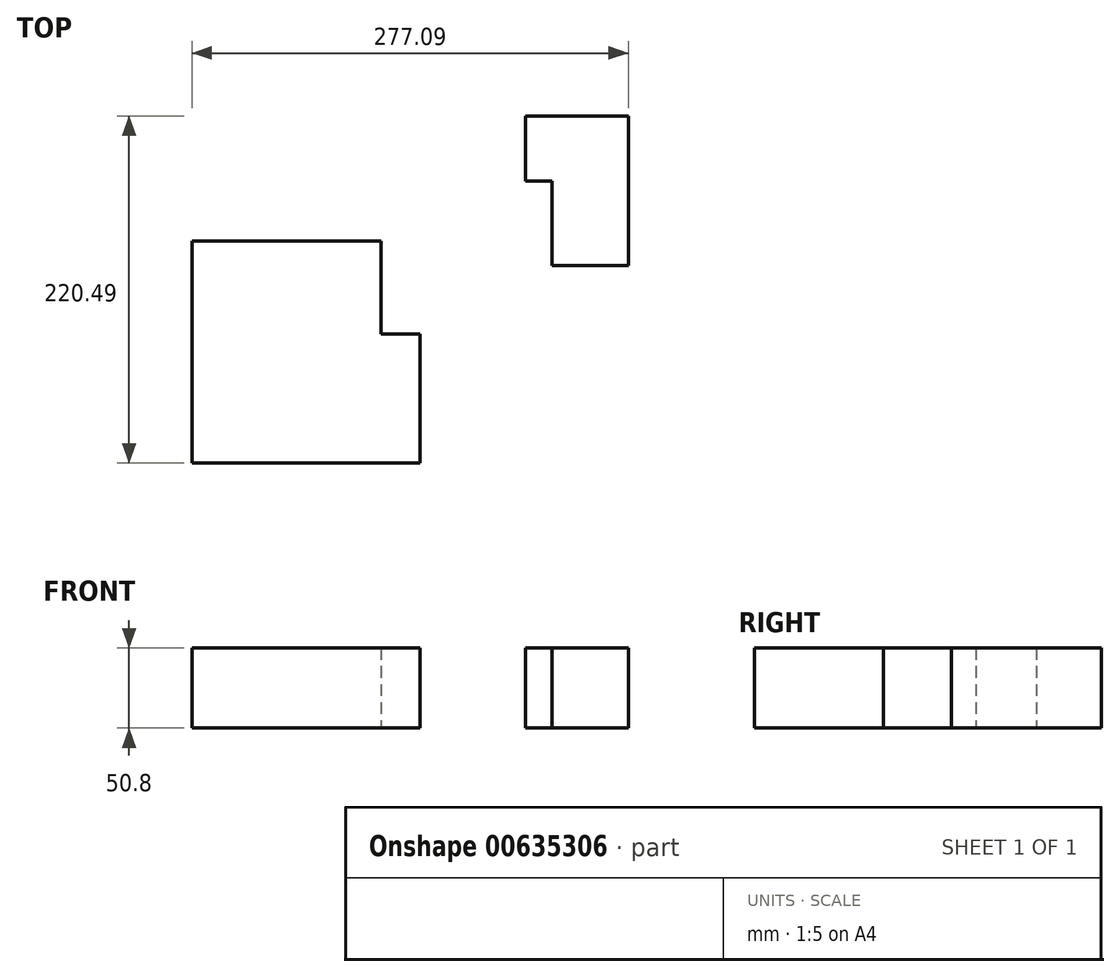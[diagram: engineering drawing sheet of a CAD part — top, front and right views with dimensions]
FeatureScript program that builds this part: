
annotation { "Feature Type Name" : "Feature", "Feature Type Description" : "" }
export const myFeature = defineFeature(function(context is Context, id is Id, definition is map)
    precondition{}
    {
        {
            var Q0;
            Q0=qCreatedBy(makeId("Top.planeOp"),FACE);
            var sketch = newSketch(context, id + "F0", { "sketchPlane" : qUnion([Q0])});
            skLineSegment(sketch, "E0.bottom", {"start": v(-75.4, 140.88) * mm, "end": v(69.35, 140.88) * mm});
            skLineSegment(sketch, "E0.top", {"start": v(-75.4, 0) * mm, "end": v(69.35, 0) * mm});
            skLineSegment(sketch, "E0.left", {"start": v(-75.4, 140.88) * mm, "end": v(-75.4, 0) * mm});
            skLineSegment(sketch, "E0.right", {"start": v(69.35, 140.88) * mm, "end": v(69.35, 0) * mm});
            skLineSegment(sketch, "E1.bottom", {"start": v(44.54, 179.13) * mm, "end": v(153.1, 179.13) * mm});
            skLineSegment(sketch, "E1.top", {"start": v(44.54, 81.94) * mm, "end": v(153.1, 81.94) * mm});
            skLineSegment(sketch, "E1.left", {"start": v(44.54, 179.13) * mm, "end": v(44.54, 81.94) * mm});
            skLineSegment(sketch, "E1.right", {"start": v(153.1, 179.13) * mm, "end": v(153.1, 81.94) * mm});
            skLineSegment(sketch, "E2.bottom", {"start": v(136.56, 220.49) * mm, "end": v(201.7, 220.49) * mm});
            skLineSegment(sketch, "E2.top", {"start": v(136.56, 125.37) * mm, "end": v(201.7, 125.37) * mm});
            skLineSegment(sketch, "E2.left", {"start": v(136.56, 220.49) * mm, "end": v(136.56, 125.37) * mm});
            skLineSegment(sketch, "E2.right", {"start": v(201.7, 220.49) * mm, "end": v(201.7, 125.37) * mm});
            skSolve(sketch);
        }
        {
            var Q0;
            {var subQ1=sQuery(id+"F0.wireOp",EDGE,"E0.top");Q0=makeQuery(id+"F0.imprint","IMPRINT",FACE,{"disambiguationData":[TD([[makeQuery(id+"F0.imprint","IMPRINT",EDGE,{"derivedFrom":subQ1}),1.0]])]});}
            var Q1;
            {var subQ4=sQuery(id+"F0.wireOp",EDGE,"E2.bottom");Q1=makeQuery(id+"F0.imprint","IMPRINT",FACE,{"disambiguationData":[TD([[makeQuery(id+"F0.imprint","IMPRINT",EDGE,{"derivedFrom":subQ4}),-1.0]])]});}
            extrude(context, id + "F1", {"entities" : qUnion([Q0, Q1]), "depth" : 50.8 * mm, "offsetDistance" : 25.4 * mm});
        }
    });
